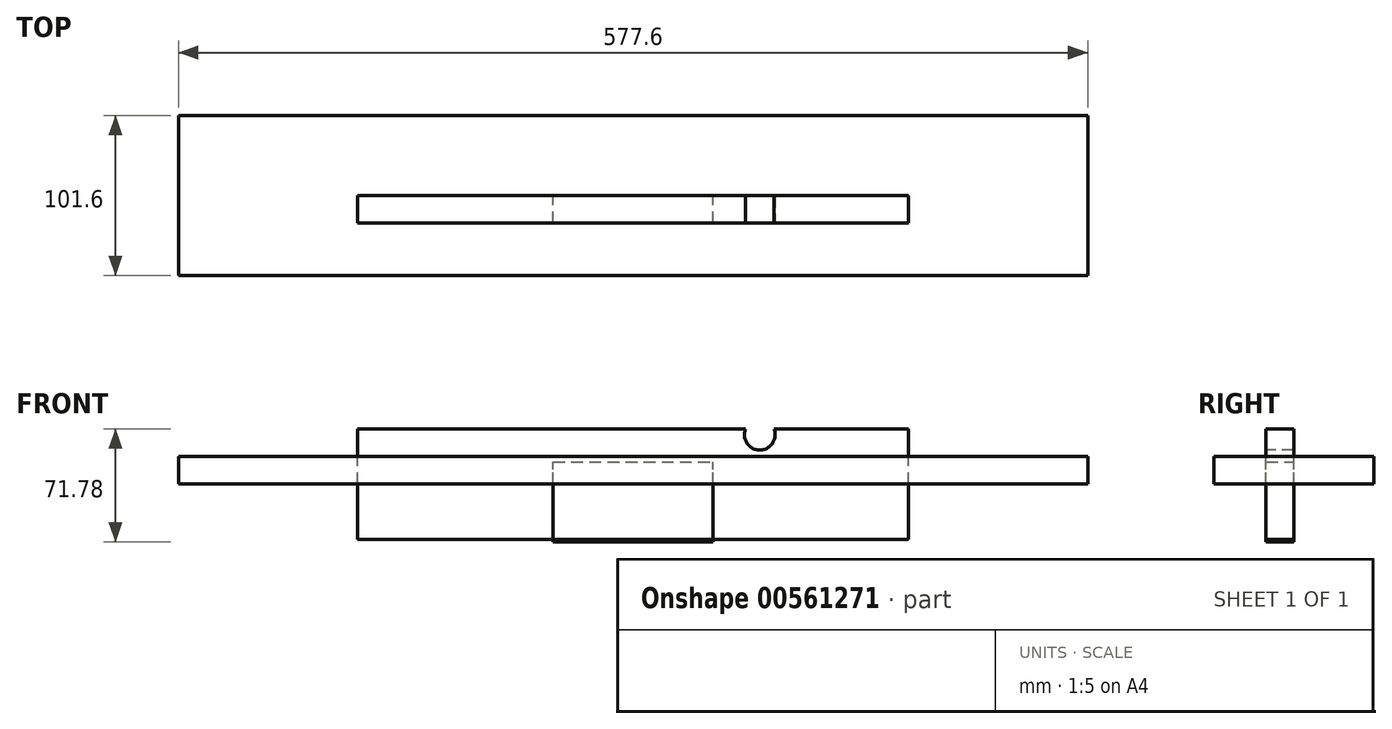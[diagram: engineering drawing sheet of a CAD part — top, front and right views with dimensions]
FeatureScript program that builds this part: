
annotation { "Feature Type Name" : "Feature", "Feature Type Description" : "" }
export const myFeature = defineFeature(function(context is Context, id is Id, definition is map)
    precondition{}
    {
        {
            var Q0;
            Q0=qCreatedBy(makeId("Front.planeOp"),FACE);
            var sketch = newSketch(context, id + "F0", { "sketchPlane" : qUnion([Q0])});
            skLineSegment(sketch, "E0.bottom", {"start": v(-175, -35) * mm, "end": v(175, -35) * mm});
            skLineSegment(sketch, "E0.top", {"start": v(-175, 35) * mm, "end": v(175, 35) * mm});
            skLineSegment(sketch, "E0.left", {"start": v(-175, -35) * mm, "end": v(-175, 35) * mm});
            skLineSegment(sketch, "E0.right", {"start": v(175, -35) * mm, "end": v(175, 35) * mm});
            skPoint(sketch, "E0.middle", {"position": v(0, 0) * mm});
            skSolve(sketch);
        }
        {
            var Q0;
            Q0 = qSketchRegion(id + "F0", true);
            extrude(context, id + "F1", {"entities" : qUnion([Q0]), "depth" : 17.6 * mm, "offsetDistance" : 25 * mm});
        }
        {
            var Q0;
            Q0=makeQuery(id+"F1.opExtrude","CAP_FACE",FACE,{"disambiguationData":[OSD([sQuery(id+"F0.wireOp",EDGE,"E0.bottom"),sQuery(id+"F0.wireOp",EDGE,"E0.top"),sQuery(id+"F0.wireOp",EDGE,"E0.left"),sQuery(id+"F0.wireOp",EDGE,"E0.right")])],"isStart":false});
            var sketch = newSketch(context, id + "F2", { "sketchPlane" : qUnion([Q0])});
            skCircle(sketch, "E1", {"center": v(80.41, 31.39) * mm, "radius": 9.75 * mm});
            skSolve(sketch);
        }
        {
            var Q0;
            Q0 = qSketchRegion(id + "F2", true);
            extrude(context, id + "F3", {"entities" : qUnion([Q0]), "operationType" : NewBodyOperationType.REMOVE, "oppositeDirection" : true, "depth" : 17.6 * mm, "offsetDistance" : 25 * mm});
        }
        {
            var Q0;
            Q0=qCreatedBy(makeId("Front.planeOp"),FACE);
            var sketch = newSketch(context, id + "F4", { "sketchPlane" : qUnion([Q0])});
            skLineSegment(sketch, "E2.bottom", {"start": v(-50.8, -36.78) * mm, "end": v(50.8, -36.78) * mm});
            skLineSegment(sketch, "E2.top", {"start": v(-50.8, 14.02) * mm, "end": v(50.8, 14.02) * mm});
            skLineSegment(sketch, "E2.left", {"start": v(-50.8, -36.78) * mm, "end": v(-50.8, 14.02) * mm});
            skLineSegment(sketch, "E2.right", {"start": v(50.8, -36.78) * mm, "end": v(50.8, 14.02) * mm});
            skPoint(sketch, "E2.middle", {"position": v(0, -11.38) * mm});
            skSolve(sketch);
        }
        {
            var Q0;
            Q0=makeQuery(id+"F4.imprint","IMPRINT",FACE,{"disambiguationData":[TD([[makeQuery(id+"F4.imprint","IMPRINT",EDGE,{"derivedFrom":sQuery(id+"F4.wireOp",EDGE,"E2.bottom")}),1.0]])]});
            extrude(context, id + "F5", {"entities" : qUnion([Q0]), "depth" : 17.6 * mm, "offsetDistance" : 25 * mm});
        }
        {
            var Q0;
            Q0=qCreatedBy(makeId("Top.planeOp"),FACE);
            var sketch = newSketch(context, id + "F6", { "sketchPlane" : qUnion([Q0])});
            skLineSegment(sketch, "E3.bottom", {"start": v(-288.8, 50.8) * mm, "end": v(288.8, 50.8) * mm});
            skLineSegment(sketch, "E3.top", {"start": v(-288.8, -50.8) * mm, "end": v(288.8, -50.8) * mm});
            skLineSegment(sketch, "E3.left", {"start": v(-288.8, 50.8) * mm, "end": v(-288.8, -50.8) * mm});
            skLineSegment(sketch, "E3.right", {"start": v(288.8, 50.8) * mm, "end": v(288.8, -50.8) * mm});
            skPoint(sketch, "E3.middle", {"position": v(0, 0) * mm});
            skSolve(sketch);
        }
        {
            var Q0;
            Q0=makeQuery(id+"F6.imprint","IMPRINT",FACE,{"disambiguationData":[TD([[makeQuery(id+"F6.imprint","IMPRINT",EDGE,{"derivedFrom":sQuery(id+"F6.wireOp",EDGE,"E3.bottom")}),-1.0]])]});
            extrude(context, id + "F7", {"entities" : qUnion([Q0]), "depth" : 17.6 * mm, "offsetDistance" : 25 * mm});
        }
    });
